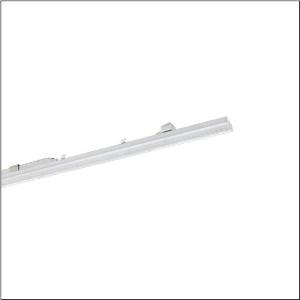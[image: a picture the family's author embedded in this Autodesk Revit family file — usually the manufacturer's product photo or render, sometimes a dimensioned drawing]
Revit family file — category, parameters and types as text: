
# Revit family: tl_l_5wd7a8d0b2c5
name_source: partatom
category: Lighting Fixtures
units: mm (PartAtom-declared; Revit-internal decimal feet)

## family parameters
Cut with Voids When Loaded = No
Host = Face
Light Source = No
Part Type = Normal
Room Calculation Point = No
Round Connector Dimension = Use Diameter
Shared = No

## types (1)
- --- (1 x LED, 9800 lm, 63.3 W, 4000K)
    Apparent Load = 63 VA
    CIE Flux Codes = 49 84 98 100 100
    Color Rendering = 80
    Color Temperature = 4000K
    Default Elevation = 1800 mm
    Description = TL L, luminaire insert, of sheet steel, galvanised, coil coated, white, length: 1.500mm, width: 66mm, height: 67mm, micro fuse,LED rated luminous flux: 9.800lm, light colour: 840, control gear: DALI, with terminal, 5-pole, mains connection: 230..240V, AC, 50/60Hz, rated input power: 63W, primary optical cover: cover, of PMMA, light emission: direct distribution, protection rating (complete): as luminaire, insulation class (complete): insulation class I (protective earthing), certification: CE, impact resistance: IK06, permissible ambient temperature for indoor applications: -25..+35°C, packaging unit: 1 piece
    Height = 120 mm
    Lamp = 1 x LED
    Lamp Light Flux = 9800 lm
    Lamp Power = 63.3 W
    Lamp count = 1
    Length = 1690 mm
    Luminous efficacy = 155 lm/W
    Manufacturer = Siteco
    ModVariant = No
    Model = 5WD7A8D0B2C5
    Mounting Place = Ceiling
    Mounting Type = Pendant
    Number of Poles = 1
    OnlyDefault = Yes
    Power Factor = 1
    Product Name = TL L
    Product group = luminaire insert
    ProductGroupID = 901
    Protection Class = Protection class I
    Protection Degree = Degree of protection
    RLX_Detail_Level = 1
    RLX_Emergency_Light_Flux = 0 lm
    RLX_Emergency_Type = 0
    RLX_Emergency_Type_DB = No
    RlxData = <blob elided: 17289 chars, md5=cd9bde1a>
    Socket = socket
    Standby Power = 0 W
    System Light Flux = 9800 lm
    System Power = 63 W
    Type Comments = factory setting: luminous flux: 100 % | dim-lin: 254 | 420 mA
    Type Image = l_1294382.jpg
    URL = http://relux.com
    VarID = @adj_031267
    Voltage = 0 V
    Weight = 0.00 kg
    Width = 208 mm

## geometry (parser evidence)
native form markers: Blend x4, Sweep x11
no freeform markers — native parametric forms only
